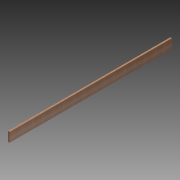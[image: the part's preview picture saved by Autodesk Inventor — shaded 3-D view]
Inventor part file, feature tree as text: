
AUTODESK INVENTOR PART (.ipt)
format: ipt  version: 2015 (Build 190159000, 159)  size: 75,264 bytes
history: native  units: in
note: dims shown in document units (in); Inventor stores cm internally (conversion verified against a paired STEP export)
features: extrude x1, sketch x1
ambient origin geometry x8: Origin, YZ Plane, XZ Plane, XY Plane, X Axis, Y Axis, Z Axis, Center Point
bodies: Solid1 (feature_tree)
feature tree (2):
  extrude  "Extrusion1"  Depth=1.5in
  sketch  "Sketch1"  dims[d0=9.25in d1=1.5in d2=160.0in d3=0.0in]
